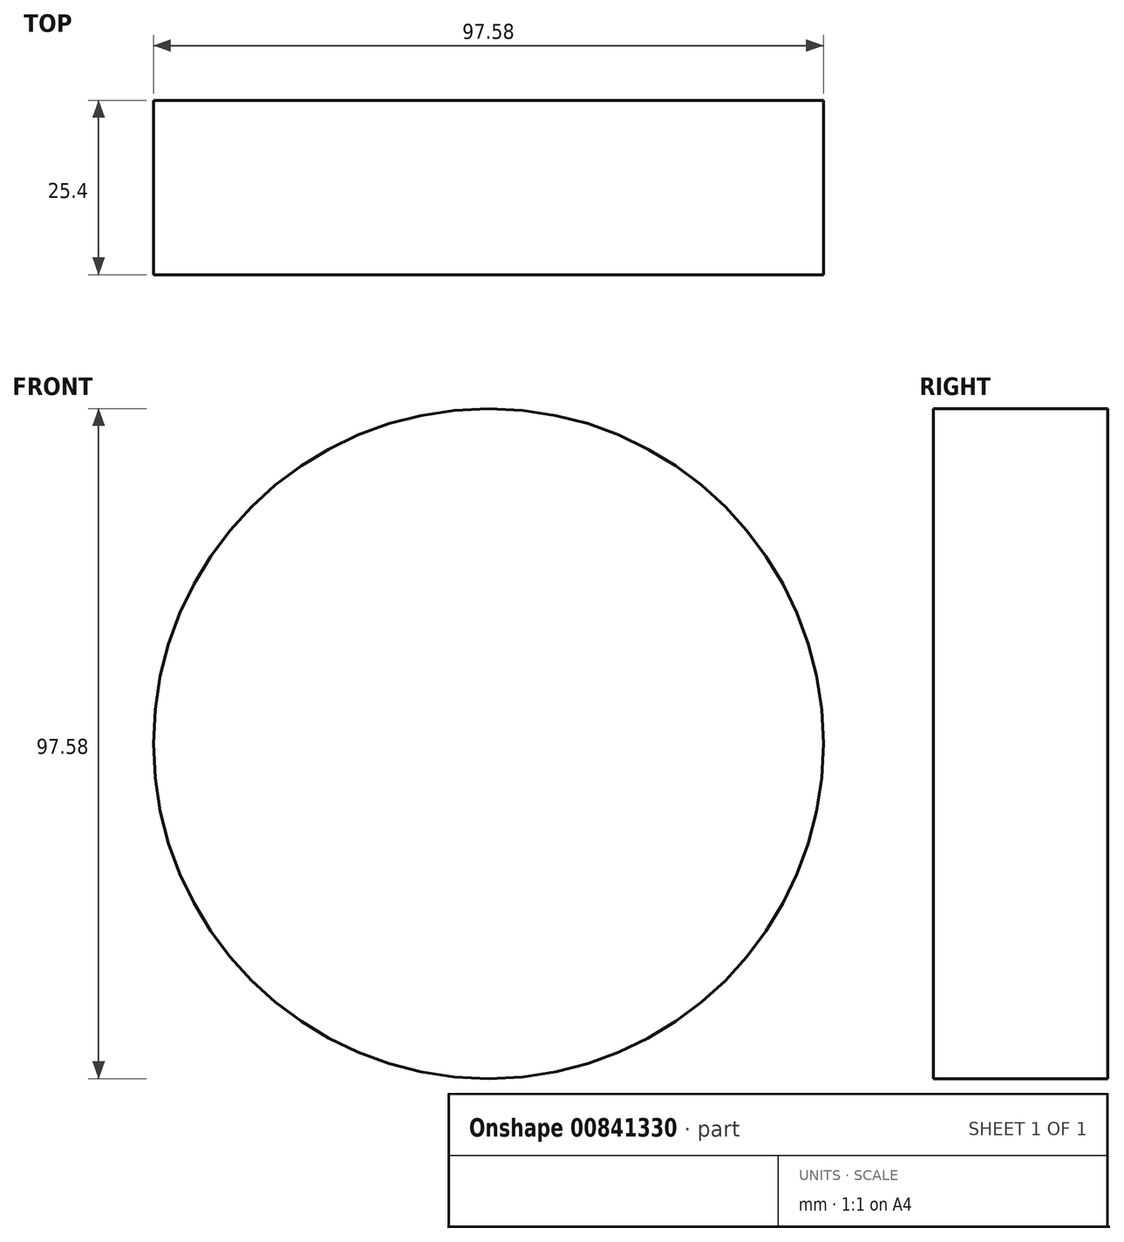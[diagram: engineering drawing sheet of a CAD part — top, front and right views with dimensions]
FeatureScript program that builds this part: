
annotation { "Feature Type Name" : "Feature", "Feature Type Description" : "" }
export const myFeature = defineFeature(function(context is Context, id is Id, definition is map)
    precondition{}
    {
        {
            var Q0;
            Q0=qCreatedBy(makeId("Front.planeOp"),FACE);
            var sketch = newSketch(context, id + "F0", { "sketchPlane" : qUnion([Q0])});
            skCircle(sketch, "E0", {"center": v(-3.8, 0) * mm, "radius": 48.79 * mm});
            skSolve(sketch);
        }
        {
            var Q0;
            Q0=makeQuery(id+"F0.imprint","IMPRINT",FACE,{"disambiguationData":[TD([[makeQuery(id+"F0.imprint","IMPRINT",EDGE,{"derivedFrom":sQuery(id+"F0.wireOp",EDGE,"E0")}),1.0]])]});
            extrude(context, id + "F1", {"entities" : qUnion([Q0]), "depth" : 25.4 * mm, "offsetDistance" : 25.4 * mm});
        }
        {
            var Q0;
            Q0=makeQuery(id+"F1.opExtrude","CAP_FACE",FACE,{"disambiguationData":[OSD([sQuery(id+"F0.wireOp",EDGE,"E0")])],"isStart":false});
            var sketch = newSketch(context, id + "F2", { "sketchPlane" : qUnion([Q0])});
            skSolve(sketch);
        }
        {
            var Q0;
            Q0=makeQuery(id+"F2.imprint","IMPRINT",FACE,{"disambiguationData":[TD([[makeQuery(id+"F2.imprint","IMPRINT",EDGE,{"derivedFrom":makeQuery(id+"F1.opExtrude","CAP_EDGE",EDGE,{"disambiguationData":[OSD([sQuery(id+"F0.wireOp",EDGE,"E0")])],"isStart":false})}),1.0]])]});
            var sketch = newSketch(context, id + "F3", { "sketchPlane" : qUnion([Q0])});
            skCircle(sketch, "E1", {"center": v(-10.9, 0) * mm, "radius": 27.11 * mm});
            skSolve(sketch);
        }
        {
            var Q0;
            Q0=sQuery(id+"F3.wireOp",EDGE,"E1");
            extrude(context, id + "F4", {"bodyType" : ExtendedToolBodyType.SURFACE, "surfaceEntities" : qUnion([Q0]), "depth" : 127 * mm, "offsetDistance" : 25.4 * mm});
        }
    });
